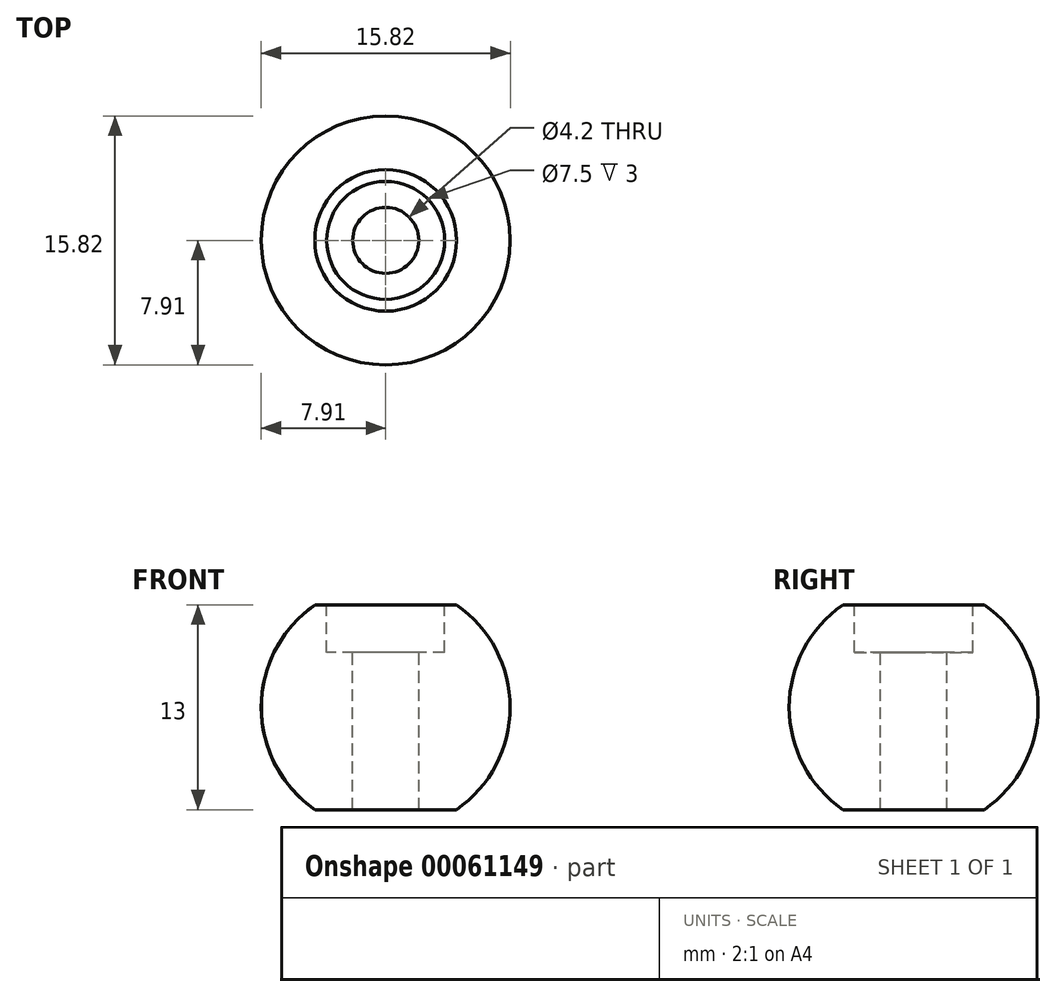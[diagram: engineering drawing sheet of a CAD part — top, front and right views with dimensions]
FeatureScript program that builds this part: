
annotation { "Feature Type Name" : "Feature", "Feature Type Description" : "" }
export const myFeature = defineFeature(function(context is Context, id is Id, definition is map)
    precondition{}
    {
        {
            var Q0;
            Q0=qCreatedBy(makeId("Front.planeOp"),FACE);
            var sketch = newSketch(context, id + "F0", { "sketchPlane" : qUnion([Q0])});
            skLineSegment(sketch, "E0", {"start": v(0, -10) * mm, "end": v(0, 10) * mm, "construction": true});
            skLineSegment(sketch, "E1", {"start": v(0, 6.5) * mm, "end": v(-4.5, 6.5) * mm});
            skLineSegment(sketch, "E2", {"start": v(0, -6.5) * mm, "end": v(-4.5, -6.5) * mm});
            skArc(sketch, "E3", {"start": v(-4.5, 6.5) * mm, "mid": v(-7.9, 0) * mm, "end": v(-4.5, -6.5) * mm});
            skLineSegment(sketch, "E4", {"start": v(0, 6.5) * mm, "end": v(0, -6.5) * mm});
            skSolve(sketch);
        }
        {
            var Q0;
            Q0=makeQuery(id+"F0.imprint","IMPRINT",FACE,{"disambiguationData":[TD([[makeQuery(id+"F0.imprint","IMPRINT",EDGE,{"derivedFrom":sQuery(id+"F0.wireOp",EDGE,"E1")}),1.0]])]});
            var Q1;
            Q1=sQuery(id+"F0.wireOp",EDGE,"E0");
            revolve(context, id + "F1", {"entities" : qUnion([Q0]), "axis" : qUnion([Q1]), "revolveType" : RevolveType.FULL});
        }
        {
            var Q0;
            Q0=makeQuery(id+"F1.opRevolve","SWEPT_FACE",FACE,{"disambiguationData":[OSD([sQuery(id+"F0.wireOp",EDGE,"E1")])]});
            var sketch = newSketch(context, id + "F2", { "sketchPlane" : qUnion([Q0])});
            skCircle(sketch, "E5", {"center": v(0, 0) * mm, "radius": 2.1 * mm});
            skCircle(sketch, "E6", {"center": v(0, 0) * mm, "radius": 3.75 * mm});
            skSolve(sketch);
        }
        {
            var Q0;
            Q0=makeQuery(id+"F2.imprint","IMPRINT",FACE,{"disambiguationData":[TD([[makeQuery(id+"F2.imprint","IMPRINT",EDGE,{"derivedFrom":sQuery(id+"F2.wireOp",EDGE,"E5")}),1.0]])]});
            extrude(context, id + "F3", {"entities" : qUnion([Q0]), "operationType" : NewBodyOperationType.REMOVE, "endBound" : BoundingType.THROUGH_ALL, "oppositeDirection" : true, "depth" : 25 * mm});
        }
        {
            var Q0;
            Q0=makeQuery(id+"F2.imprint","IMPRINT",FACE,{"disambiguationData":[TD([[makeQuery(id+"F2.imprint","IMPRINT",EDGE,{"derivedFrom":sQuery(id+"F2.wireOp",EDGE,"E5")}),-1.0]])]});
            extrude(context, id + "F4", {"entities" : qUnion([Q0]), "operationType" : NewBodyOperationType.REMOVE, "oppositeDirection" : true, "depth" : 3 * mm});
        }
    });
